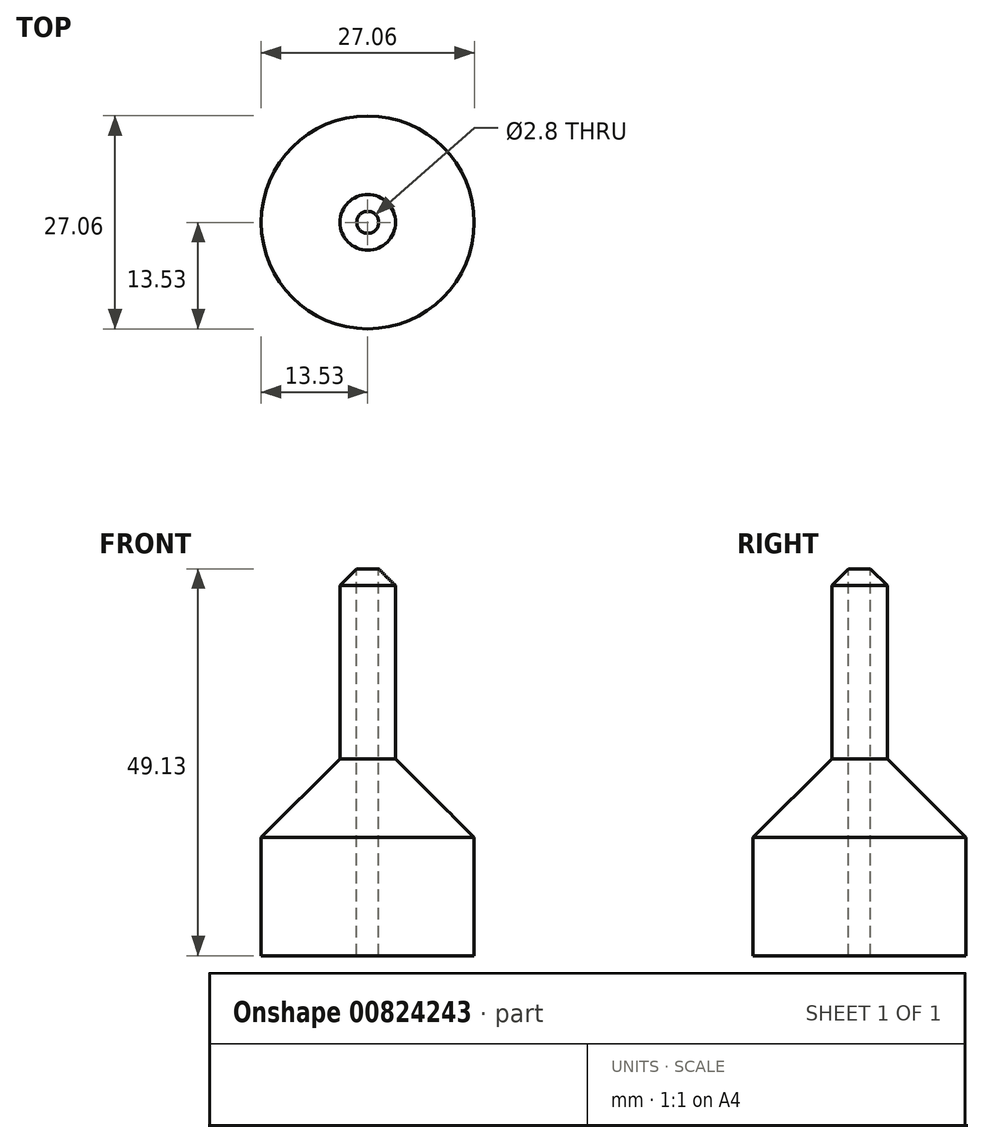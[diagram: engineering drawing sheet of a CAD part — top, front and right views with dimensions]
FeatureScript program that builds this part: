
annotation { "Feature Type Name" : "Feature", "Feature Type Description" : "" }
export const myFeature = defineFeature(function(context is Context, id is Id, definition is map)
    precondition{}
    {
        {
            var Q0;
            Q0=qCreatedBy(makeId("Top.planeOp"),FACE);
            var sketch = newSketch(context, id + "F0", { "sketchPlane" : qUnion([Q0])});
            skCircle(sketch, "E0", {"center": v(0, 0) * mm, "radius": 13.53 * mm});
            skSolve(sketch);
        }
        {
            var Q0;
            Q0 = qSketchRegion(id + "F0", true);
            extrude(context, id + "F1", {"entities" : qUnion([Q0]), "depth" : 25 * mm, "offsetDistance" : 25 * mm});
        }
        {
            var Q0;
            Q0=makeQuery(id+"F1.opExtrude","CAP_EDGE",EDGE,{"disambiguationData":[OSD([sQuery(id+"F0.wireOp",EDGE,"E0")])],"isStart":false});
            chamfer(context, id + "F2", {"entities" : qUnion([Q0]), "width" : 10 * mm, "tangentPropagation" : true});
        }
        {
            var Q0;
            Q0=makeQuery(id+"F1.opExtrude","CAP_FACE",FACE,{"disambiguationData":[OSD([sQuery(id+"F0.wireOp",EDGE,"E0")])],"isStart":false});
            extrude(context, id + "F3", {"entities" : qUnion([Q0]), "operationType" : NewBodyOperationType.ADD, "depth" : 25 * mm, "offsetDistance" : 25 * mm});
        }
        {
            var Q0;
            Q0=makeQuery(id+"F3.opExtrude","CAP_FACE",FACE,{"disambiguationData":[OSD([sQuery(id+"F0.wireOp",EDGE,"E0")])],"isStart":false});
            var sketch = newSketch(context, id + "F4", { "sketchPlane" : qUnion([Q0])});
            skCircle(sketch, "E1", {"center": v(0, 0) * mm, "radius": 1.4 * mm});
            skSolve(sketch);
        }
        {
            var Q0;
            Q0=makeQuery(id+"F4.imprint","IMPRINT",FACE,{"disambiguationData":[TD([[makeQuery(id+"F4.imprint","IMPRINT",EDGE,{"derivedFrom":sQuery(id+"F4.wireOp",EDGE,"E1")}),1.0]])]});
            extrude(context, id + "F5", {"entities" : qUnion([Q0]), "operationType" : NewBodyOperationType.REMOVE, "oppositeDirection" : true, "depth" : 100 * mm, "offsetDistance" : 25 * mm});
        }
        {
            var Q0;
            Q0=makeQuery(id+"F3.opExtrude","CAP_EDGE",EDGE,{"disambiguationData":[OSD([sQuery(id+"F0.wireOp",EDGE,"E0")])],"isStart":false});
            chamfer(context, id + "F6", {"entities" : qUnion([Q0]), "width" : 3 * mm, "tangentPropagation" : true});
        }
    });
